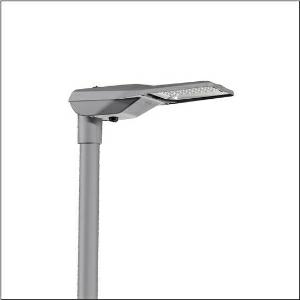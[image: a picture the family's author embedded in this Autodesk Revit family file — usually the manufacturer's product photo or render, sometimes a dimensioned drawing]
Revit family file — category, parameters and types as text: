
# Revit family: streetlight_sl_21_iq_mini___st0_5a_5xe2b31y08jb_a8c8
name_source: partatom
category: Lighting Fixtures
units: mm (PartAtom-declared; Revit-internal decimal feet)

## family parameters
Cut with Voids When Loaded = No
Host = Face
Light Source = No
Part Type = Normal
Room Calculation Point = No
Round Connector Dimension = Use Diameter
Shared = No

## types (1)
- --- (1 x LED, 11210 lm, 72.5 W, 3000K)
    Apparent Load = 73 VA
    CIE Flux Codes = 43 76 97 100 100
    Color Rendering = 70
    Color Temperature = 3000K
    Default Elevation = 1800 mm
    Description = Streetlight SL 21 iQ mini, mast luminaire, primary light control with lens, of PMMA, primary optical cover: cover, of toughened safety glass, transparent, light distribution: ST0.5a, light emission: direct distribution, primary light characteristic: asymmetric, installation type: post-top, side-entry, LED, High Power LED, rated luminous flux: 11.210lm, luminous efficacy: 155lm/W, light colour: 730, colour temperature: 3000K, control gear: iQ-Street Remote, D4i with power reduction, control: pre-setting: logarithmic dimming characteristic, Street-Remote, Auto-Match, Temp-Guard, Lumen-Switch, Night-Set, Smart-Wire, Light-Fading, Desk-Remote (wireless, voltage-free reading and setting of iQ features in the workshop via application-optimized NFC function/RFID function), optimised constant luminous flux control (CLO 2.0), mains connection: 220..240V, AC, 50/60Hz, start of lifetime: 73W, end of service life: 76W, reduction: 33W, luminaire housing, of diecast aluminium, powder-coated, SITECO metallic grey (DB 702S), corrosivity category C5 high according to DIN EN ISO 12944, please order mast flange separately, inclination adjustable: 0°, 5°, 10°, 15°, sealing non-destructively replaceable, multi-level sealing system, length: 628mm, width: 235mm, height: 110mm, mast flange for spigot size: 42mm (side-entry): 5XC10008XM4, 60/48mm (side-entry/post-top): 5XC10108XM2, 76/60mm (side-entry/post-top): 5XC10108XM1, mounting height: 4..8m, Smart Interface below and above, protection rating (complete): IP66, insulation class (complete): insulation class II (safety insulation), certification: CE, ENEC, ENEC+, VDE, impact resistance: IK10, permissible operating ambient temperature for outdoor applications: -40..+50°C, standard-compliant lighting for roads and squares, packaging unit: 1 piece

Light Distribution: ST0.5a
    Height = 110 mm
    Lamp = 1 x LED
    Lamp Light Flux = 11210 lm
    Lamp Power = 72.5 W
    Lamp count = 1
    Length = 625 mm
    Luminous efficacy = 155 lm/W
    Manufacturer = Siteco
    ModVariant = No
    Model = 5XE2B31Y08JB
    Number of Poles = 1
    OnlyDefault = Yes
    Power Factor = 1
    Product Name = Streetlight SL 21 iQ mini | ST0.5a
    Product group = mast luminaire | pylon top
    ProductGroupID = 6100
    Protection Class = Protection class II
    Protection Degree = IP 66
    RLX_Detail_Level = 1
    RLX_Emergency_Light_Flux = 0 lm
    RLX_Emergency_Type = 0
    RLX_Emergency_Type_DB = No
    RlxData = <blob elided: 104573 chars, md5=38eb2465>
    Socket = socket
    Standby Power = 0 W
    System Light Flux = 11210 lm
    System Power = 73 W
    Type Comments = factory setting: luminous flux: 100 % | dim-lin: 254 | 755 mA
    Type Image = l_1003514.jpg
    URL = http://relux.com
    VarID = @adj_115959
    Voltage = 0 V
    Weight = 0.00 kg
    Width = 234 mm

## geometry (parser evidence)
native form markers: Blend x4, Sweep x10
no freeform markers — native parametric forms only
